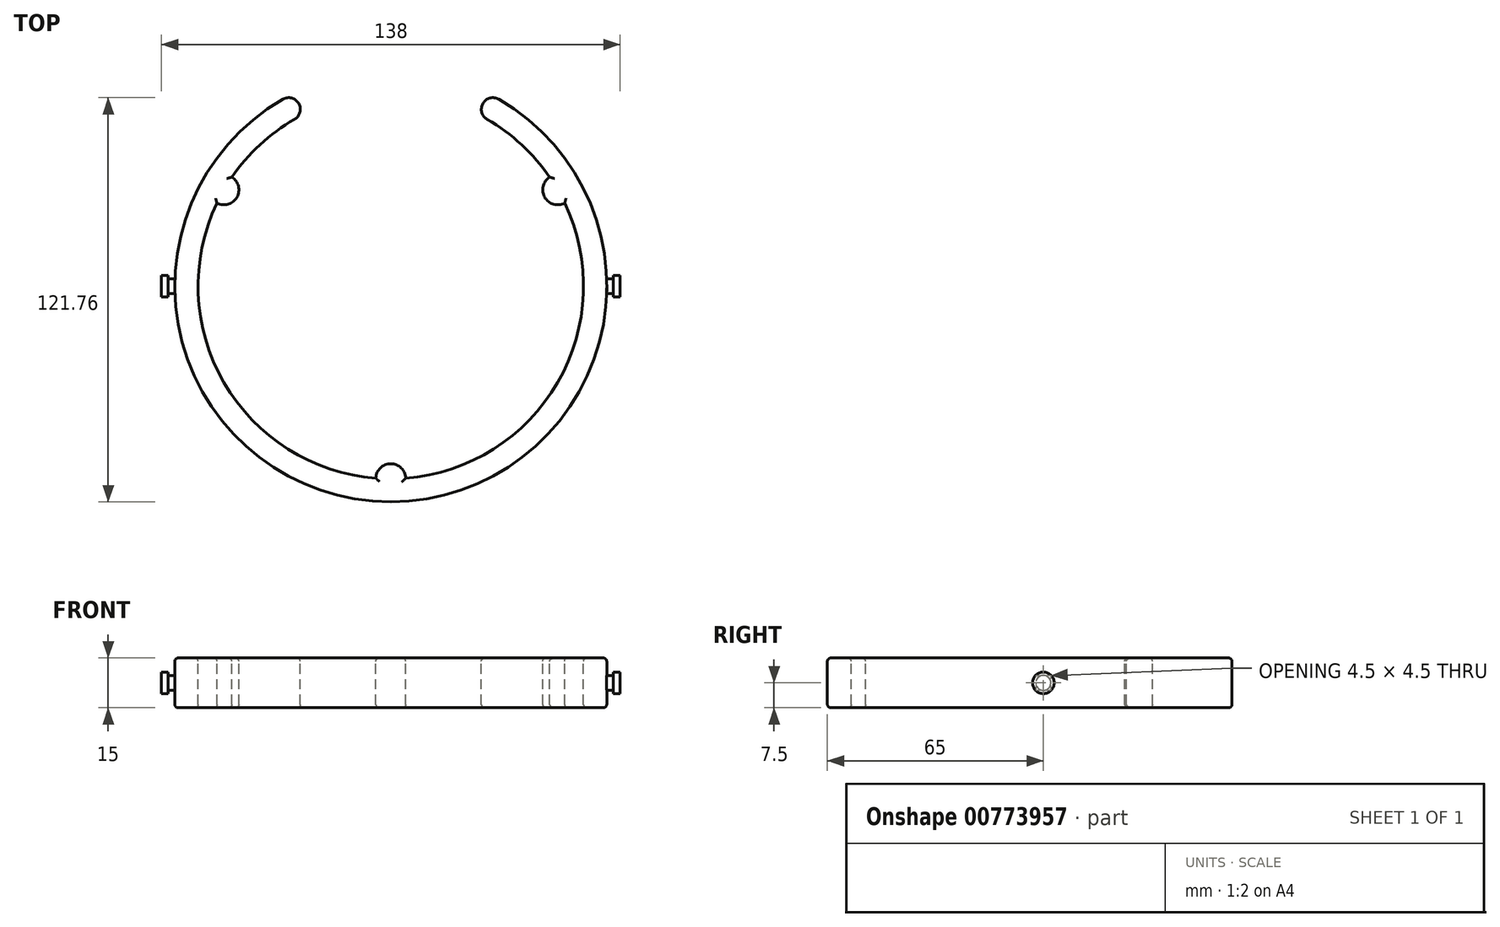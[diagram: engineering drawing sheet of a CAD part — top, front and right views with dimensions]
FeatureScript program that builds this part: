
annotation { "Feature Type Name" : "Feature", "Feature Type Description" : "" }
export const myFeature = defineFeature(function(context is Context, id is Id, definition is map)
    precondition{}
    {
        {
            var Q0;
            Q0=qCreatedBy(makeId("Top.planeOp"),FACE);
            var sketch = newSketch(context, id + "F0", { "sketchPlane" : qUnion([Q0])});
            skArc(sketch, "E0", {"start": v(4.5, -57.83) * mm, "mid": v(50.23, -29) * mm, "end": v(52.33, 25.02) * mm});
            skArc(sketch, "E1.0", {"start": v(0, -65) * mm, "mid": v(62.79, -16.82) * mm, "end": v(32.5, 56.3) * mm});
            skArc(sketch, "E2", {"start": v(32.5, 56.3) * mm, "mid": v(27.72, 55.01) * mm, "end": v(29, 50.23) * mm});
            skLineSegment(sketch, "E3", {"start": v(0, -99) * mm, "end": v(0, 78.29) * mm, "construction": true});
            skLineSegment(sketch, "E4", {"start": v(0, 0) * mm, "end": v(29, 50.23) * mm, "construction": true});
            skArc(sketch, "E5.MirrorCS", {"start": v(-4.5, -57.83) * mm, "mid": v(-50.23, -29) * mm, "end": v(-52.33, 25.02) * mm});
            skArc(sketch, "E6.MirrorCS", {"start": v(0, -65) * mm, "mid": v(-62.79, -16.82) * mm, "end": v(-32.5, 56.3) * mm});
            skArc(sketch, "E7.MirrorCS", {"start": v(-32.5, 56.3) * mm, "mid": v(-27.72, 55.01) * mm, "end": v(-29, 50.23) * mm});
            skArc(sketch, "E8", {"start": v(-4.5, -57.83) * mm, "mid": v(0, -53.5) * mm, "end": v(4.5, -57.83) * mm});
            skArc(sketch, "E9.1.0", {"start": v(52.33, 25.02) * mm, "mid": v(46.33, 26.75) * mm, "end": v(47.83, 32.8) * mm});
            skArc(sketch, "E9.2.0", {"start": v(-47.83, 32.8) * mm, "mid": v(-46.33, 26.75) * mm, "end": v(-52.33, 25.02) * mm});
            skArc(sketch, "E10.trimOffspring", {"start": v(-47.83, 32.8) * mm, "mid": v(-39.4, 42.57) * mm, "end": v(-29, 50.23) * mm});
            skArc(sketch, "E11.trimOffspring", {"start": v(47.83, 32.8) * mm, "mid": v(39.4, 42.57) * mm, "end": v(29, 50.23) * mm});
            skSolve(sketch);
        }
        {
            var Q0;
            Q0 = qSketchRegion(id + "F0", true);
            extrude(context, id + "F1", {"entities" : qUnion([Q0]), "oppositeDirection" : true, "depth" : 15 * mm, "offsetDistance" : 25 * mm});
        }
        {
            var Q0;
            Q0=qCreatedBy(makeId("Right.planeOp"),FACE);
            var sketch = newSketch(context, id + "F2", { "sketchPlane" : qUnion([Q0])});
            skCircle(sketch, "E12", {"center": v(0, -7.5) * mm, "radius": 2.25 * mm});
            skSolve(sketch);
        }
        {
            var Q0;
            Q0 = qSketchRegion(id + "F2", true);
            var Q1;
            Q1=makeQuery(id+"F1.opExtrude","SWEPT_FACE",FACE,{"disambiguationData":[OSD([sQuery(id+"F0.wireOp",EDGE,"E1.0"),sQuery(id+"F0.wireOp",EDGE,"E6.MirrorCS")])]});
            var Q2;
            Q2=makeQuery(id+"F1.opExtrude","SWEPT_FACE",FACE,{"disambiguationData":[OSD([sQuery(id+"F0.wireOp",EDGE,"E1.0"),sQuery(id+"F0.wireOp",EDGE,"E6.MirrorCS")])]});
            extrude(context, id + "F3", {"entities" : qUnion([Q0]), "depth" : 67 * mm, "endBoundEntityFace" : qUnion([Q1]), "offsetDistance" : 25 * mm, "hasSecondDirection" : true, "secondDirectionBound" : SecondDirectionBoundingType.UP_TO_SURFACE, "secondDirectionOppositeDirection" : false, "secondDirectionDepth" : 25 * mm, "secondDirectionBoundEntityFace" : qUnion([Q2])});
        }
        {
            var Q0;
            Q0=qCreatedBy(makeId("Right.planeOp"),FACE);
            var sketch = newSketch(context, id + "F4", { "sketchPlane" : qUnion([Q0])});
            skCircle(sketch, "E13", {"center": v(0, -7.5) * mm, "radius": 3.25 * mm});
            skSolve(sketch);
        }
        {
            var Q0;
            Q0 = qSketchRegion(id + "F4", true);
            var Q1;
            Q1=makeQuery(id+"F3.opExtrude","CAP_FACE",FACE,{"disambiguationData":[OSD([sQuery(id+"F2.wireOp",EDGE,"E12")])],"isStart":false});
            extrude(context, id + "F5", {"entities" : qUnion([Q0]), "operationType" : NewBodyOperationType.ADD, "depth" : 69 * mm, "offsetDistance" : 25 * mm, "hasSecondDirection" : true, "secondDirectionBound" : SecondDirectionBoundingType.UP_TO_SURFACE, "secondDirectionOppositeDirection" : false, "secondDirectionDepth" : 25 * mm, "secondDirectionBoundEntityFace" : qUnion([Q1])});
        }
        {
            var Q0;
            Q0=makeQuery(id+"F3.opExtrude","SWEPT_BODY",BODY,{"disambiguationData":[OSD([sQuery(id+"F2.wireOp",EDGE,"E12")])]});
            var Q1;
            Q1=qCreatedBy(makeId("Right.planeOp"),FACE);
            mirror(context, id + "F6", {"operationType" : NewBodyOperationType.ADD, "entities" : qUnion([Q0]), "mirrorPlane" : qUnion([Q1])});
        }
        {
            var Q0;
            Q0=makeQuery(id+"F1.opExtrude","CAP_EDGE",EDGE,{"disambiguationData":[OSD([sQuery(id+"F0.wireOp",EDGE,"E1.0"),sQuery(id+"F0.wireOp",EDGE,"E6.MirrorCS")])],"isStart":true});
            fillet(context, id + "F7", {"entities" : qUnion([Q0]), "radius" : 1 * mm, "tangentPropagation" : true, "allowEdgeOverflow" : false});
        }
        {
            var Q0;
            Q0=makeQuery(id+"F1.opExtrude","CAP_EDGE",EDGE,{"disambiguationData":[OSD([sQuery(id+"F0.wireOp",EDGE,"E1.0"),sQuery(id+"F0.wireOp",EDGE,"E6.MirrorCS")])],"isStart":false});
            fillet(context, id + "F8", {"entities" : qUnion([Q0]), "radius" : 1 * mm, "tangentPropagation" : true, "allowEdgeOverflow" : false});
        }
        {
            var Q0;
            Q0=makeQuery(id+"F1.opExtrude","CAP_EDGE",EDGE,{"disambiguationData":[OSD([sQuery(id+"F0.wireOp",EDGE,"E5.MirrorCS")])],"isStart":false});
            fillet(context, id + "F9", {"entities" : qUnion([Q0]), "radius" : 1 * mm, "tangentPropagation" : true, "allowEdgeOverflow" : false});
        }
        {
            var Q0;
            Q0=makeQuery(id+"F1.opExtrude","CAP_EDGE",EDGE,{"disambiguationData":[OSD([sQuery(id+"F0.wireOp",EDGE,"E0")])],"isStart":false});
            var Q1;
            Q1=makeQuery(id+"F1.opExtrude","CAP_EDGE",EDGE,{"disambiguationData":[OSD([sQuery(id+"F0.wireOp",EDGE,"E8")])],"isStart":false});
            var Q2;
            Q2=makeQuery(id+"F1.opExtrude","CAP_EDGE",EDGE,{"disambiguationData":[OSD([sQuery(id+"F0.wireOp",EDGE,"E5.MirrorCS")])],"isStart":true});
            var Q3;
            Q3=makeQuery(id+"F1.opExtrude","CAP_EDGE",EDGE,{"disambiguationData":[OSD([sQuery(id+"F0.wireOp",EDGE,"E0")])],"isStart":true});
            var Q4;
            Q4=makeQuery(id+"F1.opExtrude","CAP_EDGE",EDGE,{"disambiguationData":[OSD([sQuery(id+"F0.wireOp",EDGE,"E9.2.0")])],"isStart":false});
            var Q5;
            Q5=makeQuery(id+"F1.opExtrude","CAP_EDGE",EDGE,{"disambiguationData":[OSD([sQuery(id+"F0.wireOp",EDGE,"E9.2.0")])],"isStart":true});
            var Q6;
            Q6=makeQuery(id+"F1.opExtrude","CAP_EDGE",EDGE,{"disambiguationData":[OSD([sQuery(id+"F0.wireOp",EDGE,"E8")])],"isStart":true});
            var Q7;
            Q7=makeQuery(id+"F1.opExtrude","CAP_EDGE",EDGE,{"disambiguationData":[OSD([sQuery(id+"F0.wireOp",EDGE,"E9.1.0")])],"isStart":false});
            var Q8;
            Q8=makeQuery(id+"F1.opExtrude","CAP_EDGE",EDGE,{"disambiguationData":[OSD([sQuery(id+"F0.wireOp",EDGE,"E9.1.0")])],"isStart":true});
            fillet(context, id + "F10", {"entities" : qUnion([Q0, Q1, Q2, Q3, Q4, Q5, Q6, Q7, Q8]), "radius" : 1 * mm, "tangentPropagation" : true, "allowEdgeOverflow" : false});
        }
    });
